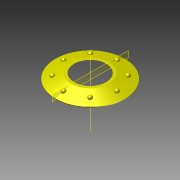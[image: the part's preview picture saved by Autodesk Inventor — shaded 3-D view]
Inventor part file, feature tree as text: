
AUTODESK INVENTOR PART (.ipt)
format: ipt  version: 2011 (Build 150239000, 239)  size: 121,856 bytes
history: native  units: in
note: dims shown in document units (in); Inventor stores cm internally (conversion verified against a paired STEP export)
features: revolve x2, sketch x2, plane x1, pattern_circular x1, other x1
ambient origin geometry x8: Origin, YZ Plane, XZ Plane, XY Plane, X Axis, Y Axis, Z Axis, Center Point
bodies: Solid1 (feature_tree)
feature tree (7):
  revolve  "Revolution1"  [1 undecoded]
  plane  "Work Plane2"
  revolve  "Revolution2"  Angle=90.0deg
  pattern_circular  "Circular Pattern1"  [2 undecoded]
  sketch  "Sketch1"  dims[d0=0.0661in d1=0.375in]
  other  "Work Axis1"
  sketch  "Sketch3"  dims[d2=0.364in d3=90.0deg d5=0.0in d6=0.0in d7=0.0in d8=0.05in d9=90.0deg d10=3.1496in d11=360.0deg]
note: 3 required parameter values undecoded (feature->parameter linkage not recoverable at this tier; creation-order binding heuristic only, values carry confidence <= 0.55)